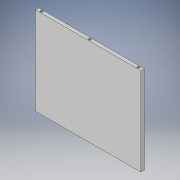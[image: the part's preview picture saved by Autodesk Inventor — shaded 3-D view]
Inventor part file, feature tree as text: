
AUTODESK INVENTOR PART (.ipt)
format: ipt  version: 2019 (Build 230136000, 136)  size: 112,128 bytes
history: native  units: mm
features: thread x3, extrude x2, sketch x2
ambient origin geometry x8: Origin, YZ Plane, XZ Plane, XY Plane, X Axis, Y Axis, Z Axis, Center Point
bodies: Solid1 (feature_tree)
feature tree (7):
  extrude  "Extrusion1"  Depth=250.0mm
  extrude  "Extrusion2"  Depth=10.0mm
  thread  "Thread1"  [1 undecoded]
  thread  "Thread2"  [1 undecoded]
  thread  "Thread3"  [1 undecoded]
  sketch  "Sketch1"  dims[d0=300.0mm d1=250.0mm]
  sketch  "Sketch4"  dims[d2=162.5mm d3=125.0mm d4=10.0mm d5=0.0mm d6=7.0mm d7=7.0mm d8=7.0mm d9=12.0mm d10=12.0mm d12=150.0mm d13=5.0mm d14=5.0mm d15=5.0mm d16=10.0mm d17=0.0mm d18=10.0mm d19=0.0mm d20=10.0mm d21=0.0mm d22=10.0mm d23=0.0mm]
note: 3 required parameter values undecoded (feature->parameter linkage not recoverable at this tier; creation-order binding heuristic only, values carry confidence <= 0.55)
